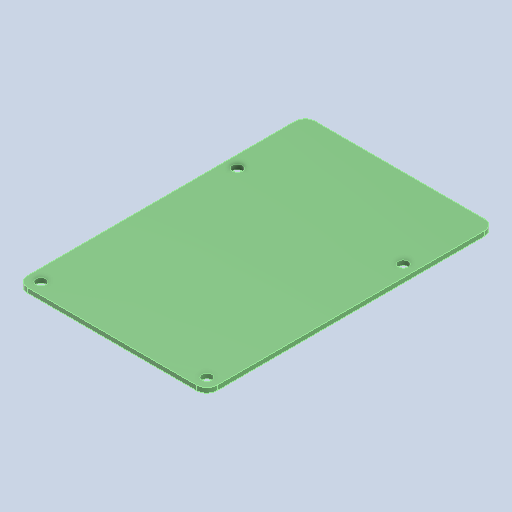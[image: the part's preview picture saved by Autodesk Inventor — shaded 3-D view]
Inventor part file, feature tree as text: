
AUTODESK INVENTOR PART (.ipt)
format: ipt  version: 2022 (Build 260153000, 153)  size: 109,568 bytes
history: native  units: mm
features: sketch x2, extrude x1, fillet x1, hole x1
ambient origin geometry x8: Origin, YZ Plane, XZ Plane, XY Plane, X Axis, Y Axis, Z Axis, Center Point
bodies: Solid1 (feature_tree)
feature tree (5):
  extrude  "Extrusion1"  Depth=56.0mm
  fillet  "Fillet1"  Radius=1.4mm
  hole  "Hole1"  [1 undecoded]
  sketch  "Sketch1"  dims[d0=85.0mm d1=56.0mm d2=1.4mm d3=0.0mm]
  sketch  "Sketch2"  dims[d4=3.0mm d5=49.0mm d6=58.0mm d7=3.5mm d8=3.5mm d9=3.0mm d10=6.0mm d11=4.0mm d12=2.0mm d13=90.0deg d14=6.0mm d15=0.0mm]
note: 1 required parameter value undecoded (feature->parameter linkage not recoverable at this tier; creation-order binding heuristic only, values carry confidence <= 0.55)
